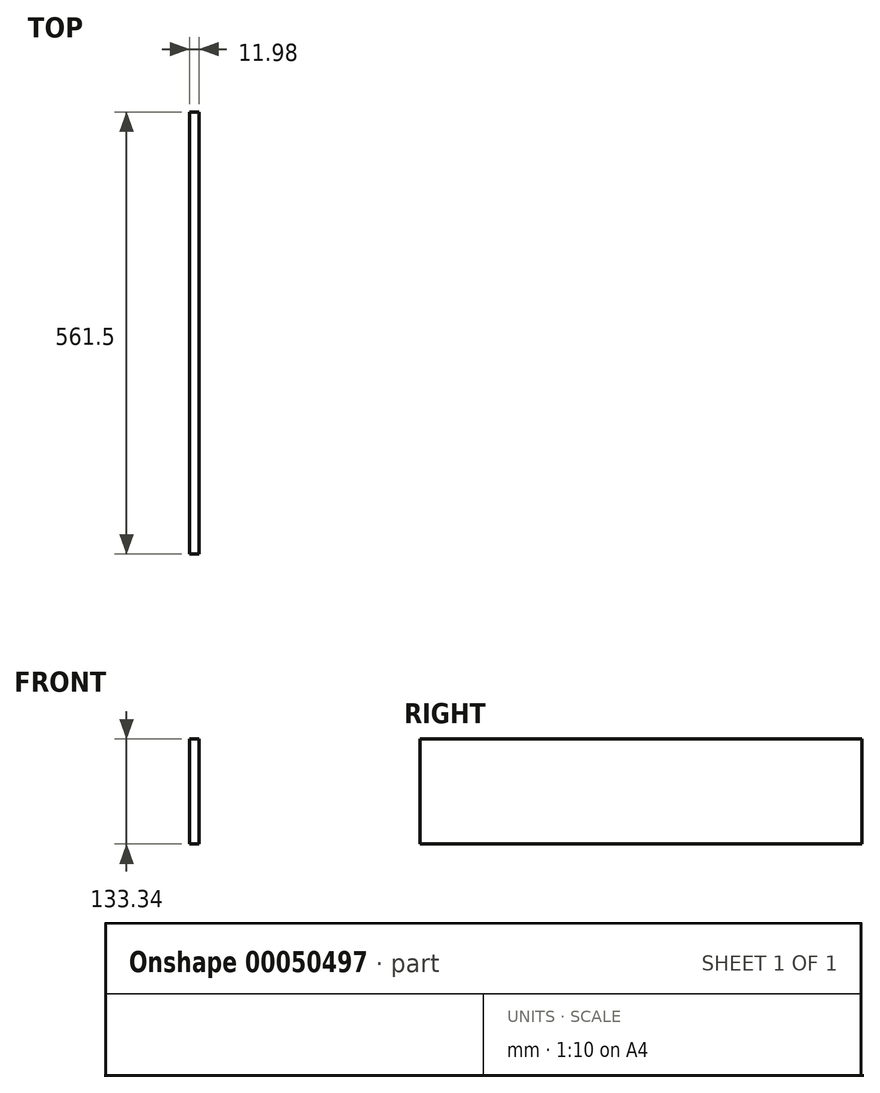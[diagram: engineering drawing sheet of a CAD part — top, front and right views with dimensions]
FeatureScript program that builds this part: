
annotation { "Feature Type Name" : "Feature", "Feature Type Description" : "" }
export const myFeature = defineFeature(function(context is Context, id is Id, definition is map)
    precondition{}
    {
        {
            var Q0;
            Q0=qCreatedBy(makeId("Right.planeOp"),FACE);
            var sketch = newSketch(context, id + "F0", { "sketchPlane" : qUnion([Q0])});
            skLineSegment(sketch, "E0.rect.bottom", {"start": v(280.75, 66.68) * mm, "end": v(-280.75, 66.68) * mm});
            skLineSegment(sketch, "E0.rect.top", {"start": v(280.75, -66.68) * mm, "end": v(-280.75, -66.68) * mm});
            skLineSegment(sketch, "E0.rect.left", {"start": v(280.75, 66.68) * mm, "end": v(280.75, -66.68) * mm});
            skLineSegment(sketch, "E0.rect.right", {"start": v(-280.75, 66.68) * mm, "end": v(-280.75, -66.68) * mm});
            skPoint(sketch, "E0.rect.middle", {"position": v(0, 0) * mm});
            skSolve(sketch);
        }
        {
            var Q0;
            Q0 = qSketchRegion(id + "F0", true);
            extrude(context, id + "F1", {"entities" : qUnion([Q0]), "endBound" : BoundingType.SYMMETRIC, "depth" : 12 * mm});
        }
    });
